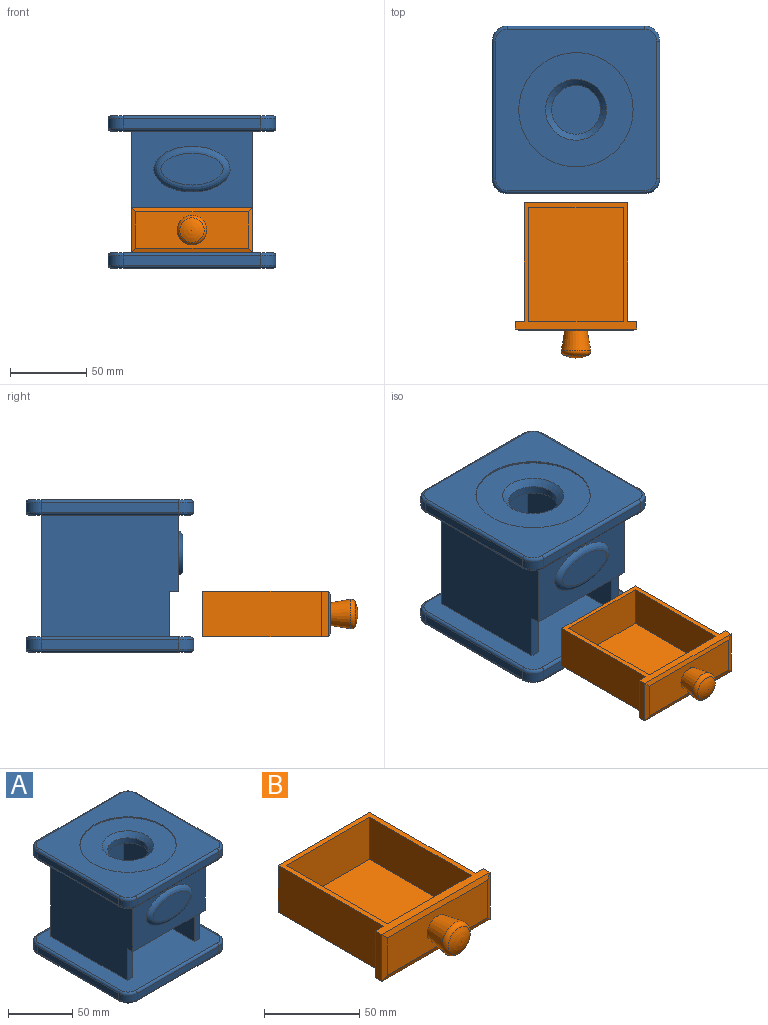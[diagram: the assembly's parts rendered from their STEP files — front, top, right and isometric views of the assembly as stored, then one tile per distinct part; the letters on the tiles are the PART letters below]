
ASSEMBLY  parts=2 mates=2
PART A: 70 faces, bbox 111.7x111.7x100.1 mm
  f0: plane 90x80mm, normal (1,0,0), area 7020mm2, adj f2,f3,f4,f30,f57,f58
  f1: plane 90x80mm, normal (-1,0,0), area 7020mm2, adj f2,f3,f4,f30,f56,f57
  f2: plane 80.07x50.07mm, normal (0,-1,0), area 2821.9mm2, adj f0,f1,f30,f57,f69
  f3: plane 80x80mm, normal (0,1,0), area 6400mm2, adj f0,f1,f4,f30
  f4: plane 106x106mm, normal (0,0,1), area 9765.1mm2, adj f0,f1,f3,f13,f14,f15,f16,f17
  f5: plane 90x6mm, normal (-1,0,0), area 540mm2, adj f9,f12,f13,f21
  f6: plane 90x6mm, normal (0,1,0), area 540mm2, adj f9,f10,f17,f25
  f7: plane 90x6mm, normal (1,0,0), area 540mm2, adj f10,f11,f20,f28
  f8: plane 90x6mm, normal (0,-1,0), area 540mm2, adj f11,f12,f16,f24
  f9: cylinder r=10mm len=10mm, axis (0,0,-1), area 94.2mm2, adj f5,f6,f15,f23
  f10: cylinder r=10mm len=10mm, axis (0,0,1), area 94.2mm2, adj f6,f7,f19,f27
  f11: cylinder r=10mm len=10mm, axis (0,0,-1), area 94.2mm2, adj f7,f8,f18,f26
  f12: cylinder r=10mm len=10mm, axis (0,0,1), area 94.2mm2, adj f5,f8,f14,f22
  f13: cylinder r=2mm len=90mm, axis (0,-1,0), area 282.7mm2, adj f4,f5,f14,f15
  f14: torus R=8mm, axis (0,0,-1), area 45.8mm2, adj f4,f12,f13,f16
  f15: torus R=8mm, axis (0,0,-1), area 45.8mm2, adj f4,f9,f13,f17
  f16: cylinder r=2mm len=90mm, axis (1,0,0), area 282.7mm2, adj f4,f8,f14,f18
  f17: cylinder r=2mm len=90mm, axis (-1,0,0), area 282.7mm2, adj f4,f6,f15,f19
  f18: torus R=8mm, axis (0,0,-1), area 45.8mm2, adj f4,f11,f16,f20
  f19: torus R=8mm, axis (0,0,-1), area 45.8mm2, adj f4,f10,f17,f20
  f20: cylinder r=2mm len=90mm, axis (0,1,0), area 282.7mm2, adj f4,f7,f18,f19
  f21: cylinder r=2mm len=90mm, axis (0,1,0), area 282.7mm2, adj f5,f22,f23,f29
  f22: torus R=8mm, axis (0,0,-1), area 45.8mm2, adj f12,f21,f24,f29
  f23: torus R=8mm, axis (0,0,-1), area 45.8mm2, adj f9,f21,f25,f29
  f24: cylinder r=2mm len=90mm, axis (-1,0,0), area 282.7mm2, adj f8,f22,f26,f29
  f25: cylinder r=2mm len=90mm, axis (1,0,0), area 282.7mm2, adj f6,f23,f27,f29
  f26: torus R=8mm, axis (0,0,-1), area 45.8mm2, adj f11,f24,f28,f29
  f27: torus R=8mm, axis (0,0,-1), area 45.8mm2, adj f10,f25,f28,f29
  f28: cylinder r=2mm len=90mm, axis (0,-1,0), area 282.7mm2, adj f7,f26,f27,f29
  f29: plane 106x106mm, normal (0,0,-1), area 11181.1mm2, adj f21,f22,f23,f24,f25,f26,f27,f28
  f30: plane 106x106mm, normal (0,0,-1), area 3981.1mm2, adj f0,f1,f2,f3,f39,f40,f41,f42
  f31: plane 90x6mm, normal (-1,0,0), area 540mm2, adj f35,f38,f39,f47
  f32: plane 90x6mm, normal (0,1,0), area 540mm2, adj f35,f36,f43,f51
  f33: plane 90x6mm, normal (1,0,0), area 540mm2, adj f36,f37,f46,f54
  f34: plane 90x6mm, normal (0,-1,0), area 540mm2, adj f37,f38,f42,f50
  f35: cylinder r=10mm len=10mm, axis (0,0,1), area 94.2mm2, adj f31,f32,f41,f49
  f36: cylinder r=10mm len=10mm, axis (0,0,-1), area 94.2mm2, adj f32,f33,f45,f53
  f37: cylinder r=10mm len=10mm, axis (0,0,1), area 94.2mm2, adj f33,f34,f44,f52
  f38: cylinder r=10mm len=10mm, axis (0,0,-1), area 94.2mm2, adj f31,f34,f40,f48
  f39: cylinder r=2mm len=90mm, axis (0,-1,0), area 282.7mm2, adj f30,f31,f40,f41
  f40: torus R=8mm, axis (0,0,1), area 45.8mm2, adj f30,f38,f39,f42
  f41: torus R=8mm, axis (0,0,1), area 45.8mm2, adj f30,f35,f39,f43
  f42: cylinder r=2mm len=90mm, axis (1,0,0), area 282.7mm2, adj f30,f34,f40,f44
  f43: cylinder r=2mm len=90mm, axis (-1,0,0), area 282.7mm2, adj f30,f32,f41,f45
  f44: torus R=8mm, axis (0,0,1), area 45.8mm2, adj f30,f37,f42,f46
  f45: torus R=8mm, axis (0,0,1), area 45.8mm2, adj f30,f36,f43,f46
  f46: cylinder r=2mm len=90mm, axis (0,1,0), area 282.7mm2, adj f30,f33,f44,f45
  f47: cylinder r=2mm len=90mm, axis (0,1,0), area 282.7mm2, adj f31,f48,f49,f55
  f48: torus R=8mm, axis (0,0,1), area 45.8mm2, adj f38,f47,f50,f55
  f49: torus R=8mm, axis (0,0,1), area 45.8mm2, adj f35,f47,f51,f55
  f50: cylinder r=2mm len=90mm, axis (-1,0,0), area 282.7mm2, adj f34,f48,f52,f55
  f51: cylinder r=2mm len=90mm, axis (1,0,0), area 282.7mm2, adj f32,f49,f53,f55
  f52: torus R=8mm, axis (0,0,1), area 45.8mm2, adj f37,f50,f54,f55
  f53: torus R=8mm, axis (0,0,1), area 45.8mm2, adj f36,f51,f54,f55
  f54: cylinder r=2mm len=90mm, axis (0,-1,0), area 282.7mm2, adj f33,f52,f53,f55
  f55: plane 106x106mm, normal (0,0,1), area 6763.2mm2, adj f47,f48,f49,f50,f51,f52,f53,f54
  f56: plane 30x6mm, normal (0,-1,0), area 180mm2, adj f1,f4,f57,f62
  f57: plane 80x6mm, normal (0,0,-1), area 480mm2, adj f0,f1,f2,f56,f58,f59
  f58: plane 30x6mm, normal (0,-1,0), area 180mm2, adj f0,f4,f57,f61
  f59: plane 68x50mm, normal (0,1,0), area 3400mm2, adj f57,f61,f62,f63
  f60: plane 80x68mm, normal (0,-1,0), area 5440mm2, adj f4,f61,f62,f63
  f61: plane 80x78mm, normal (-1,0,0), area 6240mm2, adj f4,f58,f59,f60,f63
  f62: plane 80x78mm, normal (1,0,0), area 6240mm2, adj f4,f56,f59,f60,f63
  f63: plane 78x68mm, normal (0,0,-1), area 4499.8mm2, adj f59,f60,f61,f62,f66
  f64: cylinder r=37.5mm len=75mm, axis (0,0,1), area 235.6mm2, adj f55,f65
  f65: plane 75x75mm, normal (0,0,1), area 3161.2mm2, adj f64,f67
  f66: cylinder r=16mm len=32mm, axis (0,0,1), area 502.7mm2, adj f63,f67
  f67: cone r=16mm half-angle=45deg, axis (0,0,1), area 639.8mm2, adj f65,f66
  f68: plane 40.84x20.85mm, normal (0,-1,0), area 658.6mm2, adj f69
  f69: bspline ~49.88x29.99mm, area 667mm2, adj f2,f68
PART B: 22 faces, bbox 80x102x30 mm
  f0: plane 78x30mm, normal (-1,0,0), area 2340mm2, adj f2,f3,f4,f10
  f1: plane 78x30mm, normal (1,0,0), area 2340mm2, adj f2,f3,f4,f14
  f2: plane 68x30mm, normal (0,1,0), area 2040mm2, adj f0,f1,f3,f4
  f3: plane 83x80mm, normal (0,0,1), area 1054mm2, adj f0,f1,f2,f5,f6,f7,f9,f10
  f4: plane 83x80mm, normal (0,0,-1), area 5704mm2, adj f0,f1,f2,f10,f11,f12,f14,f17
  f5: plane 75x27mm, normal (1,0,0), area 2025mm2, adj f3,f7,f8,f9
  f6: plane 75x27mm, normal (-1,0,0), area 2025mm2, adj f3,f7,f8,f9
  f7: plane 62x27mm, normal (0,-1,0), area 1674mm2, adj f3,f5,f6,f8
  f8: plane 75x62mm, normal (0,0,1), area 4650mm2, adj f5,f6,f7,f9
  f9: plane 62x27mm, normal (0,1,0), area 1674mm2, adj f3,f5,f6,f8
  f10: plane 30x6mm, normal (0,1,0), area 180mm2, adj f0,f3,f4,f11
  f11: plane 30x5mm, normal (-1,0,0), area 150mm2, adj f3,f4,f10,f15
  f12: plane 30x5mm, normal (1,0,0), area 150mm2, adj f3,f4,f14,f18
  f13: plane 74x24mm, normal (0,-1,0), area 1599.3mm2, adj f15,f16,f17,f18,f19
  f14: plane 30x6mm, normal (0,1,0), area 180mm2, adj f1,f3,f4,f12
  f15: plane 30x3mm, normal (-0.32,-0.95,0), area 85.4mm2, adj f11,f13,f16,f17
  f16: plane 80x3mm, normal (0,-0.95,0.32), area 243.5mm2, adj f3,f13,f15,f18
  f17: plane 80x3mm, normal (0,-0.95,-0.32), area 243.5mm2, adj f4,f13,f15,f18
  f18: plane 30x3mm, normal (0.32,-0.95,0), area 85.4mm2, adj f12,f13,f16,f17
  f19: cone r=10mm half-angle=9.5deg, axis (0,-1,0), area 706.5mm2, adj f13,f21
  f20: sphere r=18mm, area 214.4mm2, adj f21
  f21: torus R=6.7mm, axis (0,1,0), area 220.7mm2, adj f19,f20
PLACE A t=(-45.41,-72.63,-80.87)mm fixed
PLACE B t=(-45.41,-211.47,-120.87)mm
MATE planar A.f4 <-> B.f4  axis (0,0,1) through (-45.41,-125.63,-120.87)mm
MATE planar A.f61 <-> B.f1  axis (-1,0,0) through (-11.41,-111.63,-105.87)mm
